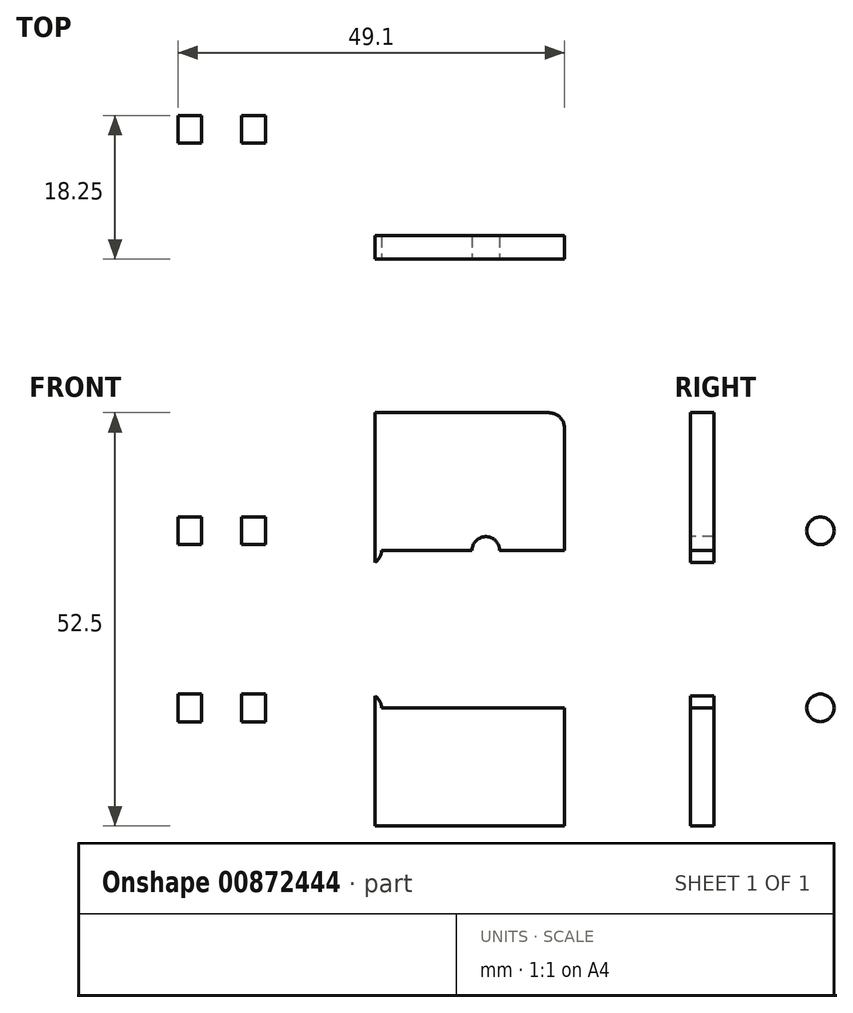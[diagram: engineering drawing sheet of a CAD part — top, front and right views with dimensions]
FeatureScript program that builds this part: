
annotation { "Feature Type Name" : "Feature", "Feature Type Description" : "" }
export const myFeature = defineFeature(function(context is Context, id is Id, definition is map)
    precondition{}
    {
        {
            var Q0;
            Q0=qCreatedBy(makeId("Top.planeOp"),FACE);
            var sketch = newSketch(context, id + "F0", { "sketchPlane" : qUnion([Q0])});
            skLineSegment(sketch, "E0", {"start": v(-1, 0) * mm, "end": v(-6.1, 0) * mm});
            skLineSegment(sketch, "E1", {"start": v(-6.1, 0) * mm, "end": v(-6.1, 30) * mm});
            skLineSegment(sketch, "E2", {"start": v(-6.1, 30) * mm, "end": v(-9.1, 30) * mm});
            skLineSegment(sketch, "E3", {"start": v(-9.1, 30) * mm, "end": v(-9.1, -3) * mm});
            skLineSegment(sketch, "E4", {"start": v(40, 0) * mm, "end": v(40, -3) * mm});
            skLineSegment(sketch, "E5", {"start": v(-9.1, -3) * mm, "end": v(40, -3) * mm});
            skLineSegment(sketch, "E6", {"start": v(-1, 0) * mm, "end": v(-1, 30) * mm});
            skLineSegment(sketch, "E7", {"start": v(-1, 0) * mm, "end": v(2, 0) * mm});
            skLineSegment(sketch, "E8", {"start": v(2, 0) * mm, "end": v(2, 30) * mm});
            skLineSegment(sketch, "E9", {"start": v(-1, 30) * mm, "end": v(2, 30) * mm});
            skLineSegment(sketch, "E10", {"start": v(2, 0) * mm, "end": v(40, 0) * mm});
            skSolve(sketch);
        }
        {
            var Q0;
            Q0=makeQuery(id+"F0.imprint","IMPRINT",FACE,{"disambiguationData":[TD([[makeQuery(id+"F0.imprint","IMPRINT",EDGE,{"derivedFrom":sQuery(id+"F0.wireOp",EDGE,"Fe5KMVJq-HbDr-zLY7-nHTo-wKJIqH0P2NG5")}),1.0]])]});
            var Q1;
            {var subQ0=sQuery(id+"F0.wireOp",EDGE,"E1");Q1=makeQuery(id+"F0.imprint","IMPRINT",FACE,{"disambiguationData":[TD([[makeQuery(id+"F0.imprint","IMPRINT",EDGE,{"derivedFrom":subQ0}),1.0]])]});}
            var Q2;
            {var subQ1=sQuery(id+"F0.wireOp",EDGE,"tfeVk5IM-x0fE-r3WH-gfiT-v8MX3nAPBLG2");Q2=makeQuery(id+"F0.imprint","IMPRINT",FACE,{"disambiguationData":[TD([[makeQuery(id+"F0.imprint","IMPRINT",EDGE,{"derivedFrom":subQ1}),-1.0]])]});}
            var Q3;
            Q3=makeQuery(id+"F0.imprint","IMPRINT",FACE,{"disambiguationData":[TD([[makeQuery(id+"F0.imprint","IMPRINT",EDGE,{"derivedFrom":sQuery(id+"F0.wireOp",EDGE,"E6")}),-1.0]])]});
            var Q4;
            Q4=sQuery(id+"F0.wireOp",EDGE,"E1");
            var Q5;
            Q5=sQuery(id+"F0.wireOp",EDGE,"E5");
            var Q6;
            Q6=sQuery(id+"F0.wireOp",EDGE,"tfeVk5IM-x0fE-r3WH-gfiT-v8MX3nAPBLG2");
            var Q7;
            Q7=sQuery(id+"F0.wireOp",EDGE,"Fe5KMVJq-HbDr-zLY7-nHTo-wKJIqH0P2NG5");
            var Q8;
            Q8=sQuery(id+"F0.wireOp",EDGE,"YAZrJ3Yh-1czD-Au5S-cxjT-P6iCzg0Z0M47");
            var Q9;
            Q9=sQuery(id+"F0.wireOp",EDGE,"E3");
            var Q10;
            Q10=sQuery(id+"F0.wireOp",EDGE,"E0");
            var Q11;
            Q11=sQuery(id+"F0.wireOp",EDGE,"E2");
            var Q12;
            Q12=sQuery(id+"F0.wireOp",EDGE,"E4");
            var Q13;
            Q13=sQuery(id+"F0.wireOp",EDGE,"1YA0MeaT-dbvA-ZEPB-I8Sy-R0e559XeavYx");
            extrude(context, id + "F1", {"entities" : qUnion([Q0, Q1, Q2, Q3]), "surfaceEntities" : qUnion([Q4, Q5, Q6, Q7, Q8, Q9, Q10, Q11, Q12, Q13]), "depth" : 52.5 * mm, "offsetDistance" : 25 * mm});
        }
        {
            var Q0;
            Q0=makeQuery(id+"F1.opExtrude","SWEPT_FACE",FACE,{"disambiguationData":[OSD([sQuery(id+"F0.wireOp",EDGE,"E3")])]});
            var sketch = newSketch(context, id + "F2", { "sketchPlane" : qUnion([Q0])});
            skLineSegment(sketch, "E11", {"start": v(3, 52.5) * mm, "end": v(3, 0) * mm});
            skLineSegment(sketch, "E12", {"start": v(-13.5, 52.5) * mm, "end": v(-13.5, 0) * mm});
            skLineSegment(sketch, "E13", {"start": v(-13.5, 52.5) * mm, "end": v(-13.5, 37.5) * mm});
            skLineSegment(sketch, "E14", {"start": v(-13.5, 26.25) * mm, "end": v(-13.5, 11.34) * mm});
            skLineSegment(sketch, "E15", {"start": v(-13.5, 0) * mm, "end": v(-13.5, 15) * mm});
            skCircle(sketch, "E16", {"center": v(-13.5, 37.5) * mm, "radius": 1.75 * mm});
            skCircle(sketch, "E17", {"center": v(-13.5, 15) * mm, "radius": 1.75 * mm});
            skSolve(sketch);
        }
        {
            var Q0;
            {var subQ0=sQuery(id+"F2.wireOp",EDGE,"E13");var subQ1=sQuery(id+"F2.wireOp",EDGE,"E12");var subQ2=makeQuery(id+"F2.imprint","INTERSECT",VERTEX,{"derivedFrom":[subQ1,subQ0]});Q0=makeQuery(id+"F2.imprint","IMPRINT",FACE,{"disambiguationData":[TD([[makeQuery(id+"F2.imprint","IMPRINT",EDGE,{"disambiguationData":[TD([[subQ2,-1.0]])],"derivedFrom":subQ1}),-1.0]])]});}
            var Q1;
            {var subQ0=sQuery(id+"F2.wireOp",EDGE,"E13");var subQ1=sQuery(id+"F2.wireOp",EDGE,"E12");var subQ2=makeQuery(id+"F2.imprint","INTERSECT",VERTEX,{"derivedFrom":[subQ1,subQ0]});Q1=makeQuery(id+"F2.imprint","IMPRINT",FACE,{"disambiguationData":[TD([[makeQuery(id+"F2.imprint","IMPRINT",EDGE,{"disambiguationData":[TD([[subQ2,-1.0]])],"derivedFrom":subQ1}),1.0]])]});}
            var Q2;
            {var subQ0=sQuery(id+"F2.wireOp",EDGE,"E15");var subQ1=sQuery(id+"F2.wireOp",EDGE,"E14");var subQ2=makeQuery(id+"F2.imprint","INTERSECT",VERTEX,{"derivedFrom":[subQ1,subQ0]});Q2=makeQuery(id+"F2.imprint","IMPRINT",FACE,{"disambiguationData":[TD([[makeQuery(id+"F2.imprint","IMPRINT",EDGE,{"disambiguationData":[TD([[subQ2,1.0]])],"derivedFrom":subQ1}),1.0]])]});}
            var Q3;
            {var subQ0=sQuery(id+"F2.wireOp",EDGE,"E15");var subQ1=sQuery(id+"F2.wireOp",EDGE,"E14");var subQ2=makeQuery(id+"F2.imprint","INTERSECT",VERTEX,{"derivedFrom":[subQ1,subQ0]});Q3=makeQuery(id+"F2.imprint","IMPRINT",FACE,{"disambiguationData":[TD([[makeQuery(id+"F2.imprint","IMPRINT",EDGE,{"disambiguationData":[TD([[subQ2,1.0]])],"derivedFrom":subQ1}),-1.0]])]});}
            var Q4;
            Q4=sQuery(id+"F2.wireOp",EDGE,"E16");
            var Q5;
            Q5=sQuery(id+"F2.wireOp",EDGE,"E17");
            extrude(context, id + "F3", {"entities" : qUnion([Q0, Q1, Q2, Q3]), "operationType" : NewBodyOperationType.REMOVE, "surfaceEntities" : qUnion([Q4, Q5]), "oppositeDirection" : true, "depth" : 25 * mm, "offsetDistance" : 25 * mm});
        }
        {
            var Q0;
            Q0=makeQuery(id+"F1.opExtrude","CAP_EDGE",EDGE,{"disambiguationData":[OSD([sQuery(id+"F0.wireOp",EDGE,"E4")])],"isStart":false});
            var Q1;
            Q1=makeQuery(id+"F1.opExtrude","SWEPT_EDGE",EDGE,{"disambiguationData":[OSD([sQuery(id+"F0.wireOp",EDGE,"E2"),sQuery(id+"F0.wireOp",EDGE,"E3")])]});
            var Q2;
            Q2=makeQuery(id+"F1.opExtrude","CAP_EDGE",EDGE,{"disambiguationData":[OSD([sQuery(id+"F0.wireOp",EDGE,"E3")])],"isStart":false});
            var Q3;
            Q3=makeQuery(id+"F1.opExtrude","CAP_EDGE",EDGE,{"disambiguationData":[OSD([sQuery(id+"F0.wireOp",EDGE,"E2")])],"isStart":false});
            fillet(context, id + "F4", {"entities" : qUnion([Q0, Q1, Q2, Q3]), "radius" : 2 * mm, "tangentPropagation" : true, "allowEdgeOverflow" : false});
        }
        {
            var Q0;
            Q0=makeQuery(id+"F1.opExtrude","SWEPT_FACE",FACE,{"disambiguationData":[OSD([sQuery(id+"F0.wireOp",EDGE,"E5")])]});
            var sketch = newSketch(context, id + "F5", { "sketchPlane" : qUnion([Q0])});
            skLineSegment(sketch, "E18", {"start": v(40, 0) * mm, "end": v(30, 0) * mm});
            skLineSegment(sketch, "E19", {"start": v(30, 0) * mm, "end": v(15, 0) * mm});
            skLineSegment(sketch, "E20", {"start": v(15, 0) * mm, "end": v(15, 52.5) * mm});
            skLineSegment(sketch, "E21", {"start": v(30, 0) * mm, "end": v(30, 52.5) * mm});
            skLineSegment(sketch, "E22", {"start": v(40, 0) * mm, "end": v(40, 15) * mm});
            skLineSegment(sketch, "E23", {"start": v(40, 15) * mm, "end": v(40, 35) * mm});
            skLineSegment(sketch, "E24", {"start": v(40, 35) * mm, "end": v(15, 35) * mm});
            skLineSegment(sketch, "E25", {"start": v(40, 15) * mm, "end": v(15, 15) * mm});
            skCircle(sketch, "E26", {"center": v(15, 35) * mm, "radius": 1.75 * mm});
            skCircle(sketch, "E27", {"center": v(15, 15) * mm, "radius": 1.75 * mm});
            skCircle(sketch, "E28", {"center": v(30, 35) * mm, "radius": 1.75 * mm});
            skPoint(sketch, "E28.centerSnap0", {"position": v(27.5, 35) * mm});
            skCircle(sketch, "E29", {"center": v(30, 15) * mm, "radius": 1.75 * mm});
            skSolve(sketch);
        }
        {
            var Q0;
            {var subQ0=sQuery(id+"F5.wireOp",EDGE,"E24");var subQ1=sQuery(id+"F5.wireOp",EDGE,"E20");var subQ2=makeQuery(id+"F5.imprint","INTERSECT",VERTEX,{"derivedFrom":[subQ1,subQ0]});Q0=makeQuery(id+"F5.imprint","IMPRINT",FACE,{"disambiguationData":[TD([[makeQuery(id+"F5.imprint","IMPRINT",EDGE,{"disambiguationData":[TD([[subQ2,1.0]])],"derivedFrom":subQ1}),-1.0]])]});}
            var Q1;
            {var subQ0=sQuery(id+"F5.wireOp",EDGE,"E20");var subQ1=makeQuery(id+"F5.imprint","INTERSECT",VERTEX,{"derivedFrom":[subQ0,sQuery(id+"F5.wireOp",EDGE,"E24")]});Q1=makeQuery(id+"F5.imprint","IMPRINT",FACE,{"disambiguationData":[TD([[makeQuery(id+"F5.imprint","IMPRINT",EDGE,{"disambiguationData":[TD([[subQ1,1.0]])],"derivedFrom":subQ0}),1.0]])]});}
            var Q2;
            {var subQ0=sQuery(id+"F5.wireOp",EDGE,"E24");var subQ1=sQuery(id+"F5.wireOp",EDGE,"E20");var subQ2=makeQuery(id+"F5.imprint","INTERSECT",VERTEX,{"derivedFrom":[subQ1,subQ0]});Q2=makeQuery(id+"F5.imprint","IMPRINT",FACE,{"disambiguationData":[TD([[makeQuery(id+"F5.imprint","IMPRINT",EDGE,{"disambiguationData":[TD([[subQ2,-1.0]])],"derivedFrom":subQ1}),-1.0]])]});}
            var Q3;
            {var subQ0=sQuery(id+"F5.wireOp",EDGE,"E24");var subQ1=sQuery(id+"F5.wireOp",EDGE,"E21");var subQ2=makeQuery(id+"F5.imprint","INTERSECT",VERTEX,{"derivedFrom":[subQ1,subQ0]});Q3=makeQuery(id+"F5.imprint","IMPRINT",FACE,{"disambiguationData":[TD([[makeQuery(id+"F5.imprint","IMPRINT",EDGE,{"disambiguationData":[TD([[subQ2,-1.0]])],"derivedFrom":subQ1}),-1.0]])]});}
            var Q4;
            {var subQ0=sQuery(id+"F5.wireOp",EDGE,"E24");var subQ1=sQuery(id+"F5.wireOp",EDGE,"E21");var subQ2=makeQuery(id+"F5.imprint","INTERSECT",VERTEX,{"derivedFrom":[subQ1,subQ0]});Q4=makeQuery(id+"F5.imprint","IMPRINT",FACE,{"disambiguationData":[TD([[makeQuery(id+"F5.imprint","IMPRINT",EDGE,{"disambiguationData":[TD([[subQ2,-1.0]])],"derivedFrom":subQ1}),1.0]])]});}
            var Q5;
            {var subQ0=sQuery(id+"F5.wireOp",EDGE,"E28");var subQ1=sQuery(id+"F5.wireOp",EDGE,"E21");var subQ2=makeQuery(id+"F5.imprint","INTERSECT",VERTEX,{"disambiguationData":[OD(0.0)],"derivedFrom":[subQ1,subQ0]});Q5=makeQuery(id+"F5.imprint","IMPRINT",FACE,{"disambiguationData":[TD([[makeQuery(id+"F5.imprint","IMPRINT",EDGE,{"disambiguationData":[TD([[subQ2,-1.0]])],"derivedFrom":subQ1}),1.0]])]});}
            var Q6;
            {var subQ0=sQuery(id+"F5.wireOp",EDGE,"E28");var subQ1=sQuery(id+"F5.wireOp",EDGE,"E21");var subQ2=makeQuery(id+"F5.imprint","INTERSECT",VERTEX,{"disambiguationData":[OD(0.0)],"derivedFrom":[subQ1,subQ0]});Q6=makeQuery(id+"F5.imprint","IMPRINT",FACE,{"disambiguationData":[TD([[makeQuery(id+"F5.imprint","IMPRINT",EDGE,{"disambiguationData":[TD([[subQ2,-1.0]])],"derivedFrom":subQ1}),-1.0]])]});}
            var Q7;
            {var subQ0=sQuery(id+"F5.wireOp",EDGE,"E25");var subQ1=sQuery(id+"F5.wireOp",EDGE,"E21");var subQ2=makeQuery(id+"F5.imprint","INTERSECT",VERTEX,{"derivedFrom":[subQ1,subQ0]});Q7=makeQuery(id+"F5.imprint","IMPRINT",FACE,{"disambiguationData":[TD([[makeQuery(id+"F5.imprint","IMPRINT",EDGE,{"disambiguationData":[TD([[subQ2,-1.0]])],"derivedFrom":subQ1}),-1.0]])]});}
            var Q8;
            {var subQ0=sQuery(id+"F5.wireOp",EDGE,"E25");var subQ1=sQuery(id+"F5.wireOp",EDGE,"E21");var subQ2=makeQuery(id+"F5.imprint","INTERSECT",VERTEX,{"derivedFrom":[subQ1,subQ0]});Q8=makeQuery(id+"F5.imprint","IMPRINT",FACE,{"disambiguationData":[TD([[makeQuery(id+"F5.imprint","IMPRINT",EDGE,{"disambiguationData":[TD([[subQ2,-1.0]])],"derivedFrom":subQ1}),1.0]])]});}
            var Q9;
            {var subQ0=sQuery(id+"F5.wireOp",EDGE,"E29");var subQ1=sQuery(id+"F5.wireOp",EDGE,"E21");var subQ2=makeQuery(id+"F5.imprint","INTERSECT",VERTEX,{"disambiguationData":[OD(0.0)],"derivedFrom":[subQ1,subQ0]});Q9=makeQuery(id+"F5.imprint","IMPRINT",FACE,{"disambiguationData":[TD([[makeQuery(id+"F5.imprint","IMPRINT",EDGE,{"disambiguationData":[TD([[subQ2,-1.0]])],"derivedFrom":subQ1}),1.0]])]});}
            var Q10;
            {var subQ0=sQuery(id+"F5.wireOp",EDGE,"E29");var subQ1=sQuery(id+"F5.wireOp",EDGE,"E21");var subQ2=makeQuery(id+"F5.imprint","INTERSECT",VERTEX,{"disambiguationData":[OD(0.0)],"derivedFrom":[subQ1,subQ0]});Q10=makeQuery(id+"F5.imprint","IMPRINT",FACE,{"disambiguationData":[TD([[makeQuery(id+"F5.imprint","IMPRINT",EDGE,{"disambiguationData":[TD([[subQ2,-1.0]])],"derivedFrom":subQ1}),-1.0]])]});}
            var Q11;
            {var subQ0=sQuery(id+"F5.wireOp",EDGE,"E25");var subQ1=sQuery(id+"F5.wireOp",EDGE,"E20");var subQ2=makeQuery(id+"F5.imprint","INTERSECT",VERTEX,{"derivedFrom":[subQ1,subQ0]});Q11=makeQuery(id+"F5.imprint","IMPRINT",FACE,{"disambiguationData":[TD([[makeQuery(id+"F5.imprint","IMPRINT",EDGE,{"disambiguationData":[TD([[subQ2,1.0]])],"derivedFrom":subQ1}),-1.0]])]});}
            var Q12;
            {var subQ0=sQuery(id+"F5.wireOp",EDGE,"E25");var subQ1=sQuery(id+"F5.wireOp",EDGE,"E20");var subQ2=makeQuery(id+"F5.imprint","INTERSECT",VERTEX,{"derivedFrom":[subQ1,subQ0]});Q12=makeQuery(id+"F5.imprint","IMPRINT",FACE,{"disambiguationData":[TD([[makeQuery(id+"F5.imprint","IMPRINT",EDGE,{"disambiguationData":[TD([[subQ2,-1.0]])],"derivedFrom":subQ1}),-1.0]])]});}
            var Q13;
            {var subQ0=sQuery(id+"F5.wireOp",EDGE,"E20");var subQ1=makeQuery(id+"F5.imprint","INTERSECT",VERTEX,{"derivedFrom":[subQ0,sQuery(id+"F5.wireOp",EDGE,"E25")]});Q13=makeQuery(id+"F5.imprint","IMPRINT",FACE,{"disambiguationData":[TD([[makeQuery(id+"F5.imprint","IMPRINT",EDGE,{"disambiguationData":[TD([[subQ1,1.0]])],"derivedFrom":subQ0}),1.0]])]});}
            extrude(context, id + "F6", {"entities" : qUnion([Q0, Q1, Q2, Q3, Q4, Q5, Q6, Q7, Q8, Q9, Q10, Q11, Q12, Q13]), "operationType" : NewBodyOperationType.REMOVE, "oppositeDirection" : true, "depth" : 25 * mm, "offsetDistance" : 25 * mm});
        }
    });
